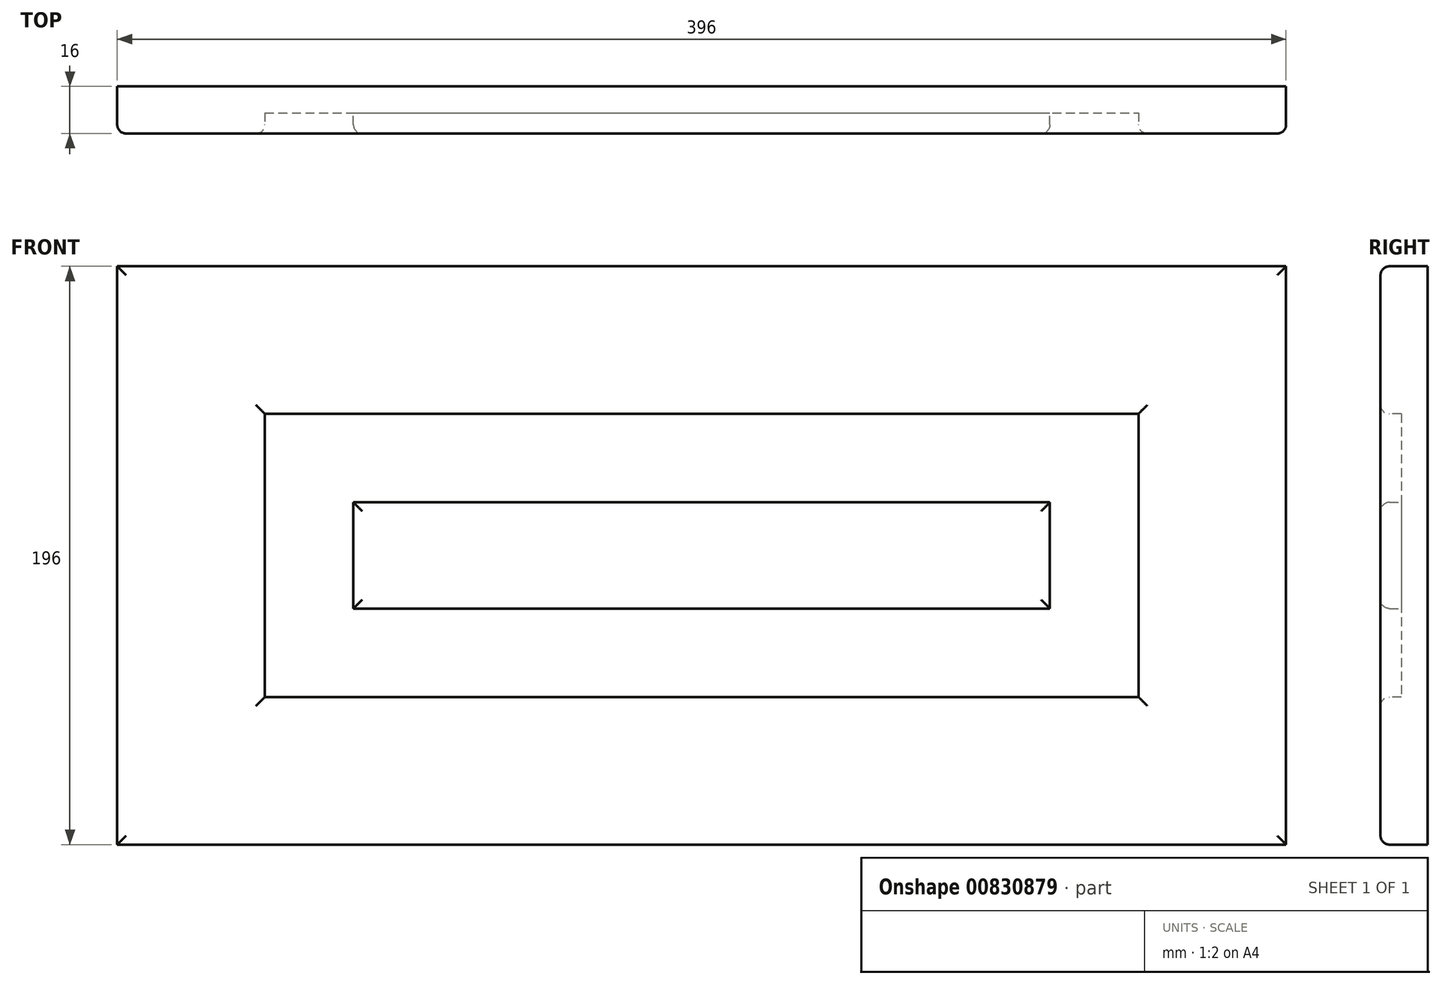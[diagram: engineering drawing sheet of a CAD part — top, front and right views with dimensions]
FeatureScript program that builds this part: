
annotation { "Feature Type Name" : "Feature", "Feature Type Description" : "" }
export const myFeature = defineFeature(function(context is Context, id is Id, definition is map)
    precondition{}
    {
        {
            var Q0;
            Q0=qCreatedBy(makeId("Front.planeOp"),FACE);
            var sketch = newSketch(context, id + "F0", { "sketchPlane" : qUnion([Q0])});
            skLineSegment(sketch, "E0.bottom", {"start": v(0, 0) * mm, "end": v(44.66, 0) * mm});
            skLineSegment(sketch, "E0.top", {"start": v(0, 33.8) * mm, "end": v(44.66, 33.8) * mm});
            skLineSegment(sketch, "E0.left", {"start": v(0, 0) * mm, "end": v(0, 33.8) * mm});
            skLineSegment(sketch, "E0.right", {"start": v(44.66, 0) * mm, "end": v(44.66, 33.8) * mm});
            skSolve(sketch);
        }
        {
            var Q0;
            Q0=makeQuery(id+"F0.imprint","IMPRINT",FACE,{"disambiguationData":[TD([[makeQuery(id+"F0.imprint","IMPRINT",EDGE,{"derivedFrom":sQuery(id+"F0.wireOp",EDGE,"E0.bottom")}),1.0]])]});
            extrude(context, id + "F1", {"entities" : qUnion([Q0]), "depth" : 16 * mm, "offsetDistance" : 25.4 * mm});
        }
        {
            var Q0;
            Q0=makeQuery(id+"F1.opExtrude","SWEPT_FACE",FACE,{"disambiguationData":[OSD([sQuery(id+"F0.wireOp",EDGE,"E0.bottom")])]});
            extrude(context, id + "F2", {"entities" : qUnion([Q0]), "operationType" : NewBodyOperationType.ADD, "oppositeDirection" : true, "depth" : 796 * mm, "offsetDistance" : 25 * mm});
        }
        {
            var Q0;
            {var subQ0=sQuery(id+"F0.wireOp",EDGE,"E0.left");Q0=makeQuery(id+"F2.boolean.opBoolean","MERGE",FACE,{"derivedFrom":[makeQuery(id+"F1.opExtrude","SWEPT_FACE",FACE,{"disambiguationData":[OSD([subQ0])]}),makeQuery(id+"F2.opExtrude","SWEPT_FACE",FACE,{"disambiguationData":[OSD([sQuery(id+"F0.wireOp",EDGE,"E0.bottom"),subQ0])]})]});}
            extrude(context, id + "F3", {"entities" : qUnion([Q0]), "operationType" : NewBodyOperationType.ADD, "oppositeDirection" : true, "depth" : 196 * mm, "offsetDistance" : 25 * mm});
        }
        {
            var Q0;
            {var subQ0=sQuery(id+"F0.wireOp",EDGE,"E0.left");var subQ1=sQuery(id+"F0.wireOp",EDGE,"E0.bottom");Q0=makeQuery(id+"F3.boolean.opBoolean","MERGE",FACE,{"derivedFrom":[makeQuery(id+"F2.boolean.opBoolean","MERGE",FACE,{"derivedFrom":[makeQuery(id+"F1.opExtrude","CAP_FACE",FACE,{"disambiguationData":[OSD([subQ1,sQuery(id+"F0.wireOp",EDGE,"E0.top"),subQ0,sQuery(id+"F0.wireOp",EDGE,"E0.right")])],"isStart":false}),makeQuery(id+"F2.opExtrude","SWEPT_FACE",FACE,{"disambiguationData":[OSD([subQ1]),TDD([makeQuery(id+"F1.opExtrude","CAP_EDGE",EDGE,{"disambiguationData":[OSD([subQ1])],"isStart":false})])]})]}),makeQuery(id+"F3.opExtrude","SWEPT_FACE",FACE,{"disambiguationData":[OSD([subQ1,subQ0]),TDD([makeQuery(id+"F2.boolean.opBoolean","MERGE",EDGE,{"derivedFrom":[makeQuery(id+"F1.opExtrude","CAP_EDGE",EDGE,{"disambiguationData":[OSD([subQ0])],"isStart":false}),makeQuery(id+"F2.opExtrude","SWEPT_EDGE",EDGE,{"disambiguationData":[OSD([subQ1,subQ0]),TDD([makeQuery(id+"F1.opExtrude","CAP_VERTEX",VERTEX,{"disambiguationData":[OSD([subQ1,subQ0])],"isStart":false})])]})]})])]})]});}
            var sketch = newSketch(context, id + "F4", { "sketchPlane" : qUnion([Q0])});
            skLineSegment(sketch, "E1.bottom", {"start": v(59.7, 646.67) * mm, "end": v(128.66, 646.67) * mm});
            skLineSegment(sketch, "E1.top", {"start": v(59.7, 152.97) * mm, "end": v(128.66, 152.97) * mm});
            skLineSegment(sketch, "E1.left", {"start": v(59.7, 646.67) * mm, "end": v(59.7, 152.97) * mm});
            skLineSegment(sketch, "E1.right", {"start": v(128.66, 646.67) * mm, "end": v(128.66, 152.97) * mm});
            skSolve(sketch);
        }
        {
            var Q0;
            Q0=makeQuery(id+"F4.imprint","IMPRINT",FACE,{"disambiguationData":[TD([[makeQuery(id+"F4.imprint","IMPRINT",EDGE,{"derivedFrom":sQuery(id+"F4.wireOp",EDGE,"E1.bottom")}),-1.0]])]});
            extrude(context, id + "F5", {"entities" : qUnion([Q0]), "operationType" : NewBodyOperationType.REMOVE, "oppositeDirection" : true, "depth" : 7 * mm, "offsetDistance" : 25 * mm});
        }
        {
            var Q0;
            Q0=makeQuery(id+"F5.boolean.opBoolean","COPY",FACE,{"derivedFrom":makeQuery(id+"F5.opExtrude","SWEPT_FACE",FACE,{"disambiguationData":[OSD([sQuery(id+"F4.wireOp",EDGE,"E1.left")])]})});
            extrude(context, id + "F6", {"entities" : qUnion([Q0]), "operationType" : NewBodyOperationType.REMOVE, "oppositeDirection" : true, "depth" : 9.7 * mm, "offsetDistance" : 25 * mm});
        }
        {
            var Q0;
            {var subQ0=sQuery(id+"F4.wireOp",EDGE,"E1.bottom");Q0=makeQuery(id+"F6.boolean.opBoolean","MERGE",FACE,{"derivedFrom":[makeQuery(id+"F5.boolean.opBoolean","COPY",FACE,{"derivedFrom":makeQuery(id+"F5.opExtrude","SWEPT_FACE",FACE,{"disambiguationData":[OSD([subQ0])]})}),makeQuery(id+"F6.opExtrude","SWEPT_FACE",FACE,{"disambiguationData":[OSD([subQ0,sQuery(id+"F4.wireOp",EDGE,"E1.left")])]})]});}
            extrude(context, id + "F7", {"entities" : qUnion([Q0]), "operationType" : NewBodyOperationType.ADD, "oppositeDirection" : true, "depth" : 99.33 * mm, "offsetDistance" : 25 * mm});
        }
        {
            var Q0;
            {var subQ0=sQuery(id+"F4.wireOp",EDGE,"E1.bottom");Q0=makeQuery(id+"F6.boolean.opBoolean","MERGE",FACE,{"derivedFrom":[makeQuery(id+"F5.boolean.opBoolean","COPY",FACE,{"derivedFrom":makeQuery(id+"F5.opExtrude","SWEPT_FACE",FACE,{"disambiguationData":[OSD([subQ0])]})}),makeQuery(id+"F6.opExtrude","SWEPT_FACE",FACE,{"disambiguationData":[OSD([subQ0,sQuery(id+"F4.wireOp",EDGE,"E1.left")])]})]});}
            extrude(context, id + "F8", {"entities" : qUnion([Q0]), "operationType" : NewBodyOperationType.REMOVE, "oppositeDirection" : true, "depth" : 99.33 * mm, "offsetDistance" : 25 * mm});
        }
        {
            var Q0;
            {var subQ0=sQuery(id+"F4.wireOp",EDGE,"E1.right");Q0=makeQuery(id+"F8.boolean.opBoolean","MERGE",FACE,{"derivedFrom":[makeQuery(id+"F5.boolean.opBoolean","COPY",FACE,{"derivedFrom":makeQuery(id+"F5.opExtrude","SWEPT_FACE",FACE,{"disambiguationData":[OSD([subQ0])]})}),makeQuery(id+"F8.opExtrude","SWEPT_FACE",FACE,{"disambiguationData":[OSD([sQuery(id+"F4.wireOp",EDGE,"E1.bottom"),subQ0])]})]});}
            extrude(context, id + "F9", {"entities" : qUnion([Q0]), "operationType" : NewBodyOperationType.REMOVE, "oppositeDirection" : true, "depth" : 17.34 * mm, "offsetDistance" : 25 * mm});
        }
        {
            var Q0;
            {var subQ0=sQuery(id+"F4.wireOp",EDGE,"E1.top");Q0=makeQuery(id+"F9.boolean.opBoolean","MERGE",FACE,{"derivedFrom":[makeQuery(id+"F6.boolean.opBoolean","MERGE",FACE,{"derivedFrom":[makeQuery(id+"F5.boolean.opBoolean","COPY",FACE,{"derivedFrom":makeQuery(id+"F5.opExtrude","SWEPT_FACE",FACE,{"disambiguationData":[OSD([subQ0])]})}),makeQuery(id+"F6.opExtrude","SWEPT_FACE",FACE,{"disambiguationData":[OSD([subQ0,sQuery(id+"F4.wireOp",EDGE,"E1.left")])]})]}),makeQuery(id+"F9.opExtrude","SWEPT_FACE",FACE,{"disambiguationData":[OSD([subQ0,sQuery(id+"F4.wireOp",EDGE,"E1.right")])]})]});}
            extrude(context, id + "F10", {"entities" : qUnion([Q0]), "operationType" : NewBodyOperationType.REMOVE, "oppositeDirection" : true, "depth" : 102.97 * mm, "offsetDistance" : 25 * mm});
        }
        {
            var Q0;
            {var subQ0=sQuery(id+"F4.wireOp",EDGE,"E1.right");var subQ1=sQuery(id+"F4.wireOp",EDGE,"E1.top");var subQ2=sQuery(id+"F4.wireOp",EDGE,"E1.left");var subQ3=sQuery(id+"F4.wireOp",EDGE,"E1.bottom");Q0=makeQuery(id+"F10.boolean.opBoolean","MERGE",FACE,{"derivedFrom":[makeQuery(id+"F9.boolean.opBoolean","MERGE",FACE,{"derivedFrom":[makeQuery(id+"F8.boolean.opBoolean","MERGE",FACE,{"derivedFrom":[makeQuery(id+"F6.boolean.opBoolean","MERGE",FACE,{"derivedFrom":[makeQuery(id+"F5.boolean.opBoolean","COPY",FACE,{"derivedFrom":makeQuery(id+"F5.opExtrude","CAP_FACE",FACE,{"disambiguationData":[OSD([subQ3,subQ1,subQ2,subQ0])],"isStart":false})}),makeQuery(id+"F6.opExtrude","SWEPT_FACE",FACE,{"disambiguationData":[OSD([subQ2]),TDD([makeQuery(id+"F5.boolean.opBoolean","COPY",EDGE,{"derivedFrom":makeQuery(id+"F5.opExtrude","CAP_EDGE",EDGE,{"disambiguationData":[OSD([subQ2])],"isStart":false})})])]})]}),makeQuery(id+"F8.opExtrude","SWEPT_FACE",FACE,{"disambiguationData":[OSD([subQ3,subQ2]),TDD([makeQuery(id+"F6.boolean.opBoolean","MERGE",EDGE,{"derivedFrom":[makeQuery(id+"F5.boolean.opBoolean","COPY",EDGE,{"derivedFrom":makeQuery(id+"F5.opExtrude","CAP_EDGE",EDGE,{"disambiguationData":[OSD([subQ3])],"isStart":false})}),makeQuery(id+"F6.opExtrude","SWEPT_EDGE",EDGE,{"disambiguationData":[OSD([subQ3,subQ2]),TDD([makeQuery(id+"F5.boolean.opBoolean","COPY",VERTEX,{"derivedFrom":makeQuery(id+"F5.opExtrude","CAP_VERTEX",VERTEX,{"disambiguationData":[OSD([subQ3,subQ2])],"isStart":false})})])]})]})])]})]}),makeQuery(id+"F9.opExtrude","SWEPT_FACE",FACE,{"disambiguationData":[OSD([subQ3,subQ0]),TDD([makeQuery(id+"F8.boolean.opBoolean","MERGE",EDGE,{"derivedFrom":[makeQuery(id+"F5.boolean.opBoolean","COPY",EDGE,{"derivedFrom":makeQuery(id+"F5.opExtrude","CAP_EDGE",EDGE,{"disambiguationData":[OSD([subQ0])],"isStart":false})}),makeQuery(id+"F8.opExtrude","SWEPT_EDGE",EDGE,{"disambiguationData":[OSD([subQ3,subQ0]),TDD([makeQuery(id+"F5.boolean.opBoolean","COPY",VERTEX,{"derivedFrom":makeQuery(id+"F5.opExtrude","CAP_VERTEX",VERTEX,{"disambiguationData":[OSD([subQ3,subQ0])],"isStart":false})})])]})]})])]})]}),makeQuery(id+"F10.opExtrude","SWEPT_FACE",FACE,{"disambiguationData":[OSD([subQ1,subQ2,subQ0]),TDD([makeQuery(id+"F9.boolean.opBoolean","MERGE",EDGE,{"derivedFrom":[makeQuery(id+"F6.boolean.opBoolean","MERGE",EDGE,{"derivedFrom":[makeQuery(id+"F5.boolean.opBoolean","COPY",EDGE,{"derivedFrom":makeQuery(id+"F5.opExtrude","CAP_EDGE",EDGE,{"disambiguationData":[OSD([subQ1])],"isStart":false})}),makeQuery(id+"F6.opExtrude","SWEPT_EDGE",EDGE,{"disambiguationData":[OSD([subQ1,subQ2]),TDD([makeQuery(id+"F5.boolean.opBoolean","COPY",VERTEX,{"derivedFrom":makeQuery(id+"F5.opExtrude","CAP_VERTEX",VERTEX,{"disambiguationData":[OSD([subQ1,subQ2])],"isStart":false})})])]})]}),makeQuery(id+"F9.opExtrude","SWEPT_EDGE",EDGE,{"disambiguationData":[OSD([subQ1,subQ0]),TDD([makeQuery(id+"F5.boolean.opBoolean","COPY",VERTEX,{"derivedFrom":makeQuery(id+"F5.opExtrude","CAP_VERTEX",VERTEX,{"disambiguationData":[OSD([subQ1,subQ0])],"isStart":false})})])]})]})])]})]});}
            var sketch = newSketch(context, id + "F11", { "sketchPlane" : qUnion([Q0])});
            skLineSegment(sketch, "E2.bottom", {"start": v(74.13, 678.73) * mm, "end": v(109.41, 678.73) * mm});
            skLineSegment(sketch, "E2.top", {"start": v(74.13, 186.63) * mm, "end": v(109.41, 186.63) * mm});
            skLineSegment(sketch, "E2.left", {"start": v(74.13, 678.73) * mm, "end": v(74.13, 186.63) * mm});
            skLineSegment(sketch, "E2.right", {"start": v(109.41, 678.73) * mm, "end": v(109.41, 186.63) * mm});
            skSolve(sketch);
        }
        {
            var Q0;
            Q0=makeQuery(id+"F11.imprint","IMPRINT",FACE,{"disambiguationData":[TD([[makeQuery(id+"F11.imprint","IMPRINT",EDGE,{"derivedFrom":sQuery(id+"F11.wireOp",EDGE,"E2.bottom")}),-1.0]])]});
            extrude(context, id + "F12", {"entities" : qUnion([Q0]), "operationType" : NewBodyOperationType.ADD, "depth" : 7 * mm, "offsetDistance" : 25 * mm});
        }
        {
            var Q0;
            Q0=makeQuery(id+"F12.opExtrude","SWEPT_FACE",FACE,{"disambiguationData":[OSD([sQuery(id+"F11.wireOp",EDGE,"E2.bottom")])]});
            extrude(context, id + "F13", {"entities" : qUnion([Q0]), "operationType" : NewBodyOperationType.ADD, "depth" : 37.27 * mm, "offsetDistance" : 25 * mm});
        }
        {
            var Q0;
            {var subQ0=sQuery(id+"F11.wireOp",EDGE,"E2.right");Q0=makeQuery(id+"F13.boolean.opBoolean","MERGE",FACE,{"derivedFrom":[makeQuery(id+"F12.opExtrude","SWEPT_FACE",FACE,{"disambiguationData":[OSD([subQ0])]}),makeQuery(id+"F13.opExtrude","SWEPT_FACE",FACE,{"disambiguationData":[OSD([sQuery(id+"F11.wireOp",EDGE,"E2.bottom"),subQ0])]})]});}
            extrude(context, id + "F14", {"entities" : qUnion([Q0]), "operationType" : NewBodyOperationType.ADD, "depth" : 6.58 * mm, "offsetDistance" : 25 * mm});
        }
        {
            var Q0;
            {var subQ0=sQuery(id+"F11.wireOp",EDGE,"E2.top");Q0=makeQuery(id+"F14.boolean.opBoolean","MERGE",FACE,{"derivedFrom":[makeQuery(id+"F12.opExtrude","SWEPT_FACE",FACE,{"disambiguationData":[OSD([subQ0])]}),makeQuery(id+"F14.opExtrude","SWEPT_FACE",FACE,{"disambiguationData":[OSD([subQ0,sQuery(id+"F11.wireOp",EDGE,"E2.right")])]})]});}
            extrude(context, id + "F15", {"entities" : qUnion([Q0]), "operationType" : NewBodyOperationType.ADD, "depth" : 106.63 * mm, "offsetDistance" : 25 * mm});
        }
        {
            var Q0;
            {var subQ0=sQuery(id+"F11.wireOp",EDGE,"E2.left");Q0=makeQuery(id+"F15.boolean.opBoolean","MERGE",FACE,{"derivedFrom":[makeQuery(id+"F13.boolean.opBoolean","MERGE",FACE,{"derivedFrom":[makeQuery(id+"F12.opExtrude","SWEPT_FACE",FACE,{"disambiguationData":[OSD([subQ0])]}),makeQuery(id+"F13.opExtrude","SWEPT_FACE",FACE,{"disambiguationData":[OSD([sQuery(id+"F11.wireOp",EDGE,"E2.bottom"),subQ0])]})]}),makeQuery(id+"F15.opExtrude","SWEPT_FACE",FACE,{"disambiguationData":[OSD([sQuery(id+"F11.wireOp",EDGE,"E2.top"),subQ0])]})]});}
            extrude(context, id + "F16", {"entities" : qUnion([Q0]), "operationType" : NewBodyOperationType.REMOVE, "oppositeDirection" : true, "depth" : 5.87 * mm, "offsetDistance" : 25 * mm});
        }
        {
            var Q0;
            Q0=makeQuery(id+"F3.opExtrude","CAP_FACE",FACE,{"disambiguationData":[OSD([sQuery(id+"F0.wireOp",EDGE,"E0.bottom"),sQuery(id+"F0.wireOp",EDGE,"E0.left")])],"isStart":false});
            extrude(context, id + "F17", {"entities" : qUnion([Q0]), "operationType" : NewBodyOperationType.ADD, "depth" : 200 * mm, "offsetDistance" : 25 * mm});
        }
        {
            var Q0;
            {var subQ0=sQuery(id+"F4.wireOp",EDGE,"E1.right");Q0=makeQuery(id+"F10.boolean.opBoolean","MERGE",FACE,{"derivedFrom":[makeQuery(id+"F9.boolean.opBoolean","COPY",FACE,{"derivedFrom":makeQuery(id+"F9.opExtrude","CAP_FACE",FACE,{"disambiguationData":[OSD([sQuery(id+"F4.wireOp",EDGE,"E1.bottom"),subQ0])],"isStart":false})}),makeQuery(id+"F10.opExtrude","SWEPT_FACE",FACE,{"disambiguationData":[OSD([sQuery(id+"F4.wireOp",EDGE,"E1.top"),subQ0])]})]});}
            extrude(context, id + "F18", {"entities" : qUnion([Q0]), "operationType" : NewBodyOperationType.REMOVE, "oppositeDirection" : true, "depth" : 200 * mm, "offsetDistance" : 25 * mm});
        }
        {
            var Q0;
            {var subQ0=sQuery(id+"F11.wireOp",EDGE,"E2.right");var subQ1=sQuery(id+"F11.wireOp",EDGE,"E2.top");Q0=makeQuery(id+"F15.boolean.opBoolean","MERGE",FACE,{"derivedFrom":[makeQuery(id+"F14.opExtrude","CAP_FACE",FACE,{"disambiguationData":[OSD([sQuery(id+"F11.wireOp",EDGE,"E2.bottom"),subQ0])],"isStart":false}),makeQuery(id+"F15.opExtrude","SWEPT_FACE",FACE,{"disambiguationData":[OSD([subQ1,subQ0]),TDD([makeQuery(id+"F14.opExtrude","CAP_EDGE",EDGE,{"disambiguationData":[OSD([subQ1,subQ0])],"isStart":false})])]})]});}
            extrude(context, id + "F19", {"entities" : qUnion([Q0]), "operationType" : NewBodyOperationType.ADD, "depth" : 200 * mm, "offsetDistance" : 25 * mm});
        }
        {
            var Q0;
            {var subQ0=sQuery(id+"F11.wireOp",EDGE,"E2.right");var subQ1=sQuery(id+"F11.wireOp",EDGE,"E2.top");Q0=makeQuery(id+"F19.boolean.opBoolean","MERGE",FACE,{"derivedFrom":[makeQuery(id+"F15.opExtrude","CAP_FACE",FACE,{"disambiguationData":[OSD([subQ1,subQ0])],"isStart":false}),makeQuery(id+"F19.opExtrude","SWEPT_FACE",FACE,{"disambiguationData":[OSD([subQ1,subQ0])]})]});}
            extrude(context, id + "F20", {"entities" : qUnion([Q0]), "operationType" : NewBodyOperationType.REMOVE, "oppositeDirection" : true, "depth" : 600 * mm, "offsetDistance" : 25 * mm});
        }
        {
            var Q0;
            {var subQ0=sQuery(id+"F4.wireOp",EDGE,"E1.right");var subQ1=sQuery(id+"F4.wireOp",EDGE,"E1.top");Q0=makeQuery(id+"F18.boolean.opBoolean","MERGE",FACE,{"derivedFrom":[makeQuery(id+"F10.boolean.opBoolean","COPY",FACE,{"derivedFrom":makeQuery(id+"F10.opExtrude","CAP_FACE",FACE,{"disambiguationData":[OSD([subQ1,sQuery(id+"F4.wireOp",EDGE,"E1.left"),subQ0])],"isStart":false})}),makeQuery(id+"F18.opExtrude","SWEPT_FACE",FACE,{"disambiguationData":[OSD([subQ1,subQ0])]})]});}
            extrude(context, id + "F21", {"entities" : qUnion([Q0]), "operationType" : NewBodyOperationType.ADD, "depth" : 600 * mm, "offsetDistance" : 25 * mm});
        }
        {
            var Q0;
            {var subQ0=sQuery(id+"F0.wireOp",EDGE,"E0.left");var subQ1=sQuery(id+"F0.wireOp",EDGE,"E0.bottom");var subQ2=makeQuery(id+"F1.opExtrude","SWEPT_EDGE",EDGE,{"disambiguationData":[OSD([subQ1,subQ0])]});Q0=makeQuery(id+"F17.boolean.opBoolean","MERGE",FACE,{"derivedFrom":[makeQuery(id+"F3.boolean.opBoolean","MERGE",FACE,{"derivedFrom":[makeQuery(id+"F1.opExtrude","SWEPT_FACE",FACE,{"disambiguationData":[OSD([subQ1])]}),makeQuery(id+"F3.opExtrude","SWEPT_FACE",FACE,{"disambiguationData":[OSD([subQ1,subQ0]),TDD([subQ2])]})]}),makeQuery(id+"F17.opExtrude","SWEPT_FACE",FACE,{"disambiguationData":[OSD([subQ1,subQ0]),TDD([makeQuery(id+"F3.opExtrude","CAP_EDGE",EDGE,{"disambiguationData":[OSD([subQ1,subQ0]),TDD([subQ2])],"isStart":false})])]})]});}
            extrude(context, id + "F22", {"entities" : qUnion([Q0]), "operationType" : NewBodyOperationType.REMOVE, "oppositeDirection" : true, "depth" : 600 * mm, "offsetDistance" : 25 * mm});
        }
        {
            var Q0;
            {var subQ0=sQuery(id+"F4.wireOp",EDGE,"E1.right");var subQ1=sQuery(id+"F4.wireOp",EDGE,"E1.top");var subQ2=makeQuery(id+"F5.boolean.opBoolean","COPY",VERTEX,{"derivedFrom":makeQuery(id+"F5.opExtrude","CAP_VERTEX",VERTEX,{"disambiguationData":[OSD([subQ1,subQ0])],"isStart":true})});var subQ3=sQuery(id+"F4.wireOp",EDGE,"E1.left");var subQ4=sQuery(id+"F0.wireOp",EDGE,"E0.left");var subQ5=sQuery(id+"F0.wireOp",EDGE,"E0.bottom");var subQ6=makeQuery(id+"F2.boolean.opBoolean","MERGE",EDGE,{"derivedFrom":[makeQuery(id+"F1.opExtrude","CAP_EDGE",EDGE,{"disambiguationData":[OSD([subQ4])],"isStart":false}),makeQuery(id+"F2.opExtrude","SWEPT_EDGE",EDGE,{"disambiguationData":[OSD([subQ5,subQ4]),TDD([makeQuery(id+"F1.opExtrude","CAP_VERTEX",VERTEX,{"disambiguationData":[OSD([subQ5,subQ4])],"isStart":false})])]})]});Q0=makeQuery(id+"F21.boolean.opBoolean","MERGE",FACE,{"derivedFrom":[makeQuery(id+"F17.boolean.opBoolean","MERGE",FACE,{"derivedFrom":[makeQuery(id+"F3.boolean.opBoolean","MERGE",FACE,{"derivedFrom":[makeQuery(id+"F2.boolean.opBoolean","MERGE",FACE,{"derivedFrom":[makeQuery(id+"F1.opExtrude","CAP_FACE",FACE,{"disambiguationData":[OSD([subQ5,sQuery(id+"F0.wireOp",EDGE,"E0.top"),subQ4,sQuery(id+"F0.wireOp",EDGE,"E0.right")])],"isStart":false}),makeQuery(id+"F2.opExtrude","SWEPT_FACE",FACE,{"disambiguationData":[OSD([subQ5]),TDD([makeQuery(id+"F1.opExtrude","CAP_EDGE",EDGE,{"disambiguationData":[OSD([subQ5])],"isStart":false})])]})]}),makeQuery(id+"F3.opExtrude","SWEPT_FACE",FACE,{"disambiguationData":[OSD([subQ5,subQ4]),TDD([subQ6])]})]}),makeQuery(id+"F17.opExtrude","SWEPT_FACE",FACE,{"disambiguationData":[OSD([subQ5,subQ4]),TDD([makeQuery(id+"F3.opExtrude","CAP_EDGE",EDGE,{"disambiguationData":[OSD([subQ5,subQ4]),TDD([subQ6])],"isStart":false})])]})]}),makeQuery(id+"F21.opExtrude","SWEPT_FACE",FACE,{"disambiguationData":[OSD([subQ1,subQ3,subQ0]),TDD([makeQuery(id+"F18.boolean.opBoolean","MERGE",EDGE,{"derivedFrom":[makeQuery(id+"F10.boolean.opBoolean","COPY",EDGE,{"derivedFrom":makeQuery(id+"F10.opExtrude","CAP_EDGE",EDGE,{"disambiguationData":[OSD([subQ1,subQ3,subQ0]),TDD([makeQuery(id+"F9.boolean.opBoolean","MERGE",EDGE,{"derivedFrom":[makeQuery(id+"F6.boolean.opBoolean","MERGE",EDGE,{"derivedFrom":[makeQuery(id+"F5.boolean.opBoolean","COPY",EDGE,{"derivedFrom":makeQuery(id+"F5.opExtrude","CAP_EDGE",EDGE,{"disambiguationData":[OSD([subQ1])],"isStart":true})}),makeQuery(id+"F6.opExtrude","SWEPT_EDGE",EDGE,{"disambiguationData":[OSD([subQ1,subQ3]),TDD([makeQuery(id+"F5.boolean.opBoolean","COPY",VERTEX,{"derivedFrom":makeQuery(id+"F5.opExtrude","CAP_VERTEX",VERTEX,{"disambiguationData":[OSD([subQ1,subQ3])],"isStart":true})})])]})]}),makeQuery(id+"F9.opExtrude","SWEPT_EDGE",EDGE,{"disambiguationData":[OSD([subQ1,subQ0]),TDD([subQ2])]})]})])],"isStart":false})}),makeQuery(id+"F18.opExtrude","SWEPT_EDGE",EDGE,{"disambiguationData":[OSD([subQ1,subQ0]),TDD([makeQuery(id+"F10.boolean.opBoolean","COPY",VERTEX,{"derivedFrom":makeQuery(id+"F10.opExtrude","CAP_VERTEX",VERTEX,{"disambiguationData":[OSD([subQ1,subQ0]),TDD([makeQuery(id+"F9.boolean.opBoolean","COPY",VERTEX,{"derivedFrom":makeQuery(id+"F9.opExtrude","CAP_VERTEX",VERTEX,{"disambiguationData":[OSD([subQ1,subQ0]),TDD([subQ2])],"isStart":false})})])],"isStart":false})})])]})]})])]})]});}
            var Q1;
            {var subQ0=sQuery(id+"F11.wireOp",EDGE,"E2.right");var subQ1=sQuery(id+"F11.wireOp",EDGE,"E2.top");var subQ2=makeQuery(id+"F12.opExtrude","CAP_VERTEX",VERTEX,{"disambiguationData":[OSD([subQ1,subQ0])],"isStart":false});var subQ3=sQuery(id+"F11.wireOp",EDGE,"E2.bottom");var subQ4=makeQuery(id+"F13.boolean.opBoolean","MERGE",EDGE,{"derivedFrom":[makeQuery(id+"F12.opExtrude","CAP_EDGE",EDGE,{"disambiguationData":[OSD([subQ0])],"isStart":false}),makeQuery(id+"F13.opExtrude","SWEPT_EDGE",EDGE,{"disambiguationData":[OSD([subQ3,subQ0]),TDD([makeQuery(id+"F12.opExtrude","CAP_VERTEX",VERTEX,{"disambiguationData":[OSD([subQ3,subQ0])],"isStart":false})])]})]});Q1=makeQuery(id+"F19.boolean.opBoolean","MERGE",FACE,{"derivedFrom":[makeQuery(id+"F15.boolean.opBoolean","MERGE",FACE,{"derivedFrom":[makeQuery(id+"F14.boolean.opBoolean","MERGE",FACE,{"derivedFrom":[makeQuery(id+"F13.boolean.opBoolean","MERGE",FACE,{"derivedFrom":[makeQuery(id+"F12.opExtrude","CAP_FACE",FACE,{"disambiguationData":[OSD([subQ3,subQ1,sQuery(id+"F11.wireOp",EDGE,"E2.left"),subQ0])],"isStart":false}),makeQuery(id+"F13.opExtrude","SWEPT_FACE",FACE,{"disambiguationData":[OSD([subQ3]),TDD([makeQuery(id+"F12.opExtrude","CAP_EDGE",EDGE,{"disambiguationData":[OSD([subQ3])],"isStart":false})])]})]}),makeQuery(id+"F14.opExtrude","SWEPT_FACE",FACE,{"disambiguationData":[OSD([subQ3,subQ0]),TDD([subQ4])]})]}),makeQuery(id+"F15.opExtrude","SWEPT_FACE",FACE,{"disambiguationData":[OSD([subQ1,subQ0]),TDD([makeQuery(id+"F14.boolean.opBoolean","MERGE",EDGE,{"derivedFrom":[makeQuery(id+"F12.opExtrude","CAP_EDGE",EDGE,{"disambiguationData":[OSD([subQ1])],"isStart":false}),makeQuery(id+"F14.opExtrude","SWEPT_EDGE",EDGE,{"disambiguationData":[OSD([subQ1,subQ0]),TDD([subQ2])]})]})])]})]}),makeQuery(id+"F19.opExtrude","SWEPT_FACE",FACE,{"disambiguationData":[OSD([subQ3,subQ1,subQ0]),TDD([makeQuery(id+"F15.boolean.opBoolean","MERGE",EDGE,{"derivedFrom":[makeQuery(id+"F14.opExtrude","CAP_EDGE",EDGE,{"disambiguationData":[OSD([subQ3,subQ0]),TDD([subQ4])],"isStart":false}),makeQuery(id+"F15.opExtrude","SWEPT_EDGE",EDGE,{"disambiguationData":[OSD([subQ1,subQ0]),TDD([makeQuery(id+"F14.opExtrude","CAP_VERTEX",VERTEX,{"disambiguationData":[OSD([subQ1,subQ0]),TDD([subQ2])],"isStart":false})])]})]})])]})]});}
            fillet(context, id + "F23", {"entities" : qUnion([Q0, Q1]), "radius" : 3 * mm, "tangentPropagation" : true, "allowEdgeOverflow" : false});
        }
    });
